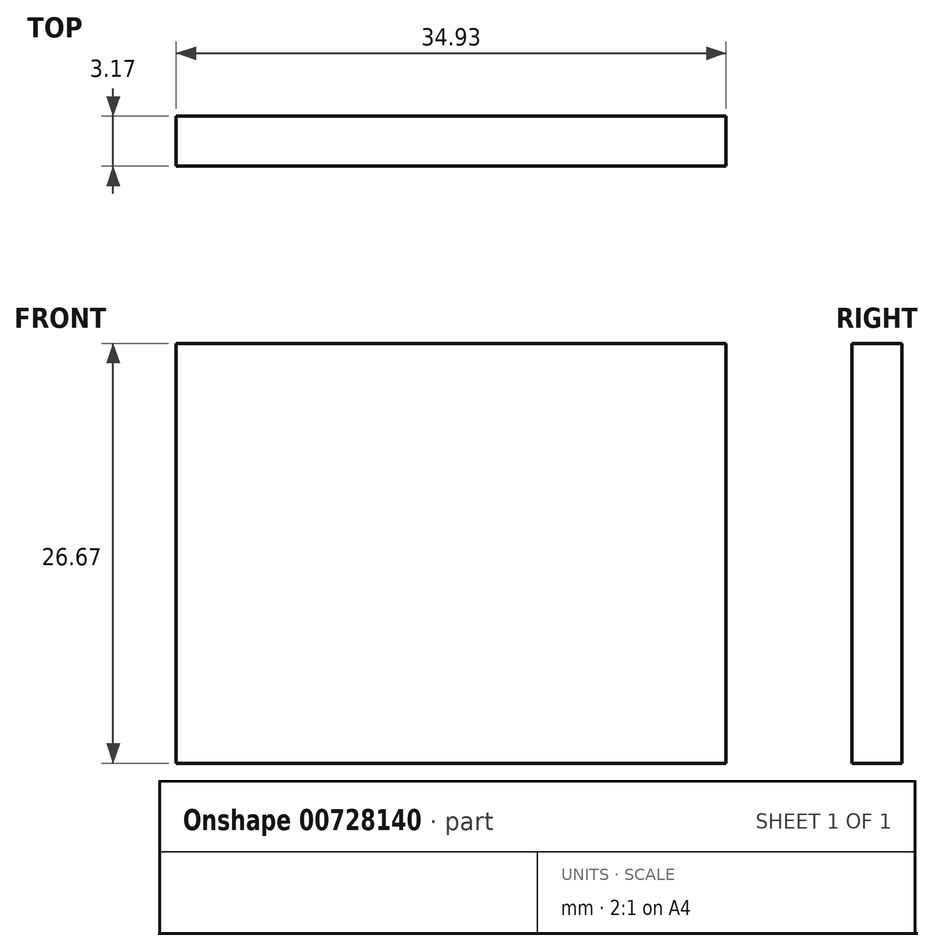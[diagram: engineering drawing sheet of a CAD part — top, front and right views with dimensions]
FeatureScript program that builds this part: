
annotation { "Feature Type Name" : "Feature", "Feature Type Description" : "" }
export const myFeature = defineFeature(function(context is Context, id is Id, definition is map)
    precondition{}
    {
        {
            var Q0;
            Q0=qCreatedBy(makeId("Front.planeOp"),FACE);
            var sketch = newSketch(context, id + "F0", { "sketchPlane" : qUnion([Q0])});
            skLineSegment(sketch, "E0.bottom", {"start": v(19.05, 38.1) * mm, "end": v(-19.05, 38.1) * mm});
            skLineSegment(sketch, "E0.top", {"start": v(19.05, -38.1) * mm, "end": v(-19.05, -38.1) * mm});
            skLineSegment(sketch, "E0.left", {"start": v(19.05, 38.1) * mm, "end": v(19.05, -38.1) * mm});
            skLineSegment(sketch, "E0.right", {"start": v(-19.05, 38.1) * mm, "end": v(-19.05, -38.1) * mm});
            skPoint(sketch, "E0.middle", {"position": v(0, 0) * mm});
            skLineSegment(sketch, "E1", {"start": v(-15.88, 38.1) * mm, "end": v(-15.88, -38.1) * mm});
            skLineSegment(sketch, "E2", {"start": v(-19.05, 29.2) * mm, "end": v(-15.88, 29.2) * mm});
            skLineSegment(sketch, "E3", {"start": v(-19.05, 20.32) * mm, "end": v(-15.88, 20.32) * mm});
            skLineSegment(sketch, "E4", {"start": v(-19.05, 11.43) * mm, "end": v(-15.88, 11.43) * mm});
            skLineSegment(sketch, "E5", {"start": v(-19.05, -1.27) * mm, "end": v(-15.88, -1.27) * mm});
            skLineSegment(sketch, "E6", {"start": v(-19.05, -13.97) * mm, "end": v(-15.88, -13.97) * mm});
            skLineSegment(sketch, "E7", {"start": v(-15.88, 11.43) * mm, "end": v(19.05, 11.43) * mm});
            skSolve(sketch);
        }
        {
            var Q0;
            {var subQ5=sQuery(id+"F0.wireOp",EDGE,"QXyYzKvK-Vf3k-rWq0-lT2y-zqTFrBfQWzn5");Q0=makeQuery(id+"F0.imprint","IMPRINT",FACE,{"disambiguationData":[TD([[makeQuery(id+"F0.imprint","IMPRINT",EDGE,{"derivedFrom":subQ5}),1.0]])]});}
            var Q1;
            {var subQ5=sQuery(id+"F0.wireOp",EDGE,"E7");Q1=makeQuery(id+"F0.imprint","IMPRINT",FACE,{"disambiguationData":[TD([[makeQuery(id+"F0.imprint","IMPRINT",EDGE,{"derivedFrom":subQ5}),1.0]])]});}
            extrude(context, id + "F1", {"entities" : qUnion([Q0, Q1]), "depth" : 3.17 * mm, "offsetDistance" : 25.4 * mm});
        }
    });
